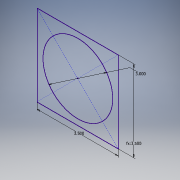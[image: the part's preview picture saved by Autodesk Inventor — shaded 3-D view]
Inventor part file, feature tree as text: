
AUTODESK INVENTOR PART (.ipt)
format: ipt  version: 2018 (Build 220112000, 112)  size: 90,112 bytes
history: native  units: in
note: dims shown in document units (in); Inventor stores cm internally (conversion verified against a paired STEP export)
features: sketch x1
ambient origin geometry x8: Origin, YZ Plane, XZ Plane, XY Plane, X Axis, Y Axis, Z Axis, Center Point
feature tree (1):
  sketch  "Sketch1"  dims[d0=3.0in d1=3.5in d2=3.5in]
